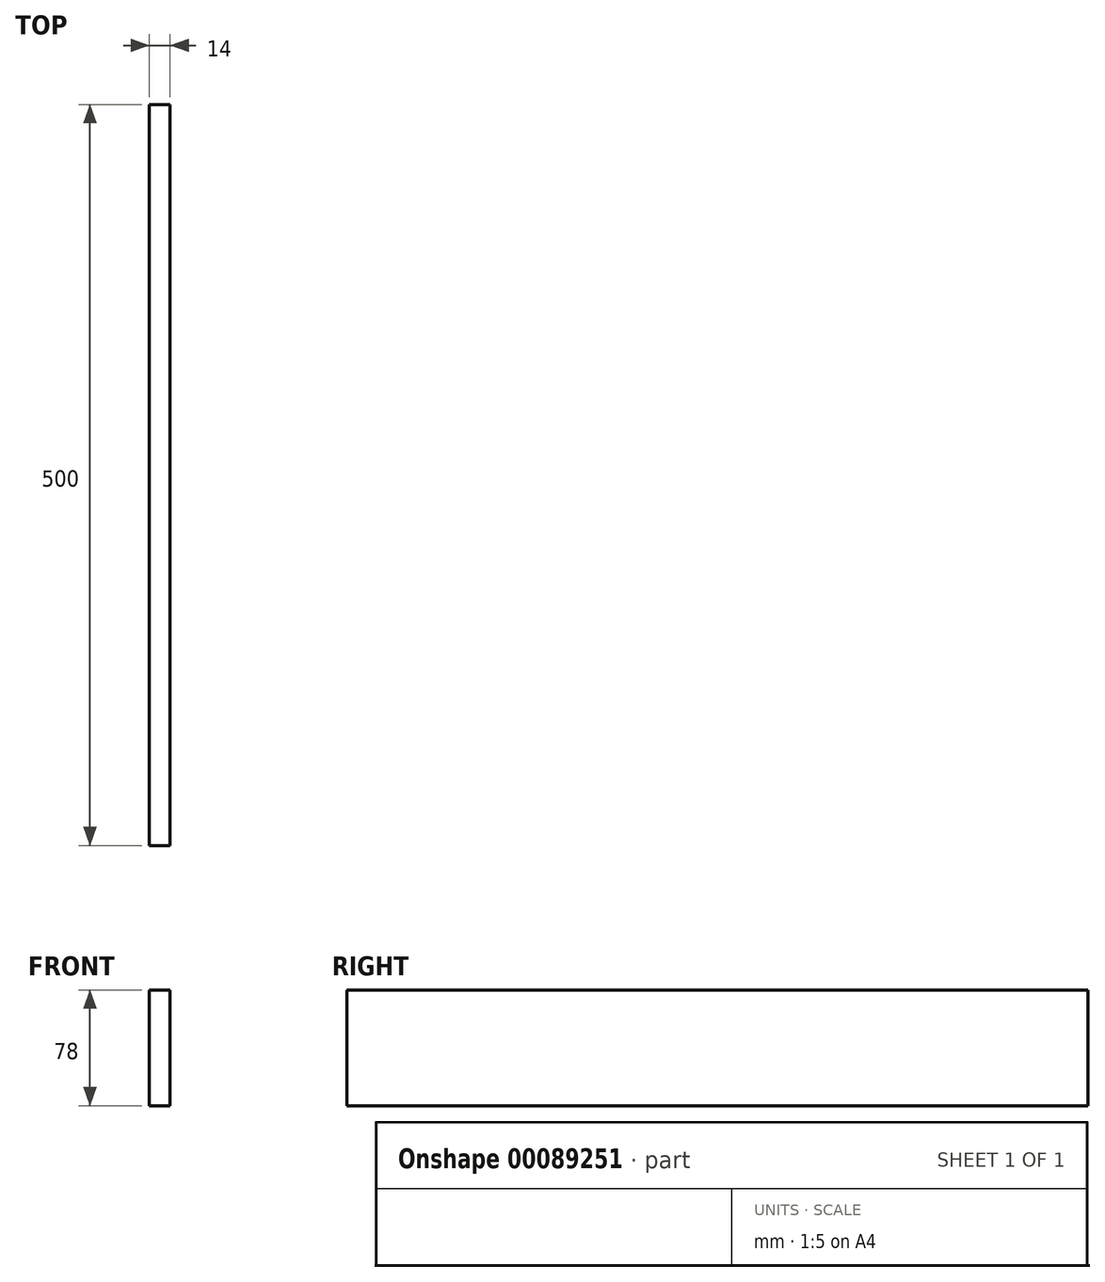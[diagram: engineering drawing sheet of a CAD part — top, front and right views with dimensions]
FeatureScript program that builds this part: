
annotation { "Feature Type Name" : "Feature", "Feature Type Description" : "" }
export const myFeature = defineFeature(function(context is Context, id is Id, definition is map)
    precondition{}
    {
        {
            var Q0;
            Q0=qCreatedBy(makeId("Front.planeOp"),FACE);
            var sketch = newSketch(context, id + "F0", { "sketchPlane" : qUnion([Q0])});
            skLineSegment(sketch, "E0.bottom", {"start": v(-7, 39) * mm, "end": v(7, 39) * mm});
            skLineSegment(sketch, "E0.top", {"start": v(-7, -39) * mm, "end": v(7, -39) * mm});
            skLineSegment(sketch, "E0.left", {"start": v(-7, 39) * mm, "end": v(-7, -39) * mm});
            skLineSegment(sketch, "E0.right", {"start": v(7, 39) * mm, "end": v(7, -39) * mm});
            skPoint(sketch, "E0.middle", {"position": v(0, 0) * mm});
            skSolve(sketch);
        }
        {
            var Q0;
            Q0=makeQuery(id+"F0.imprint","IMPRINT",FACE,{"disambiguationData":[TD([[makeQuery(id+"F0.imprint","IMPRINT",EDGE,{"derivedFrom":sQuery(id+"F0.wireOp",EDGE,"E0.bottom")}),-1.0]])]});
            extrude(context, id + "F1", {"entities" : qUnion([Q0]), "depth" : 500 * mm});
        }
    });
